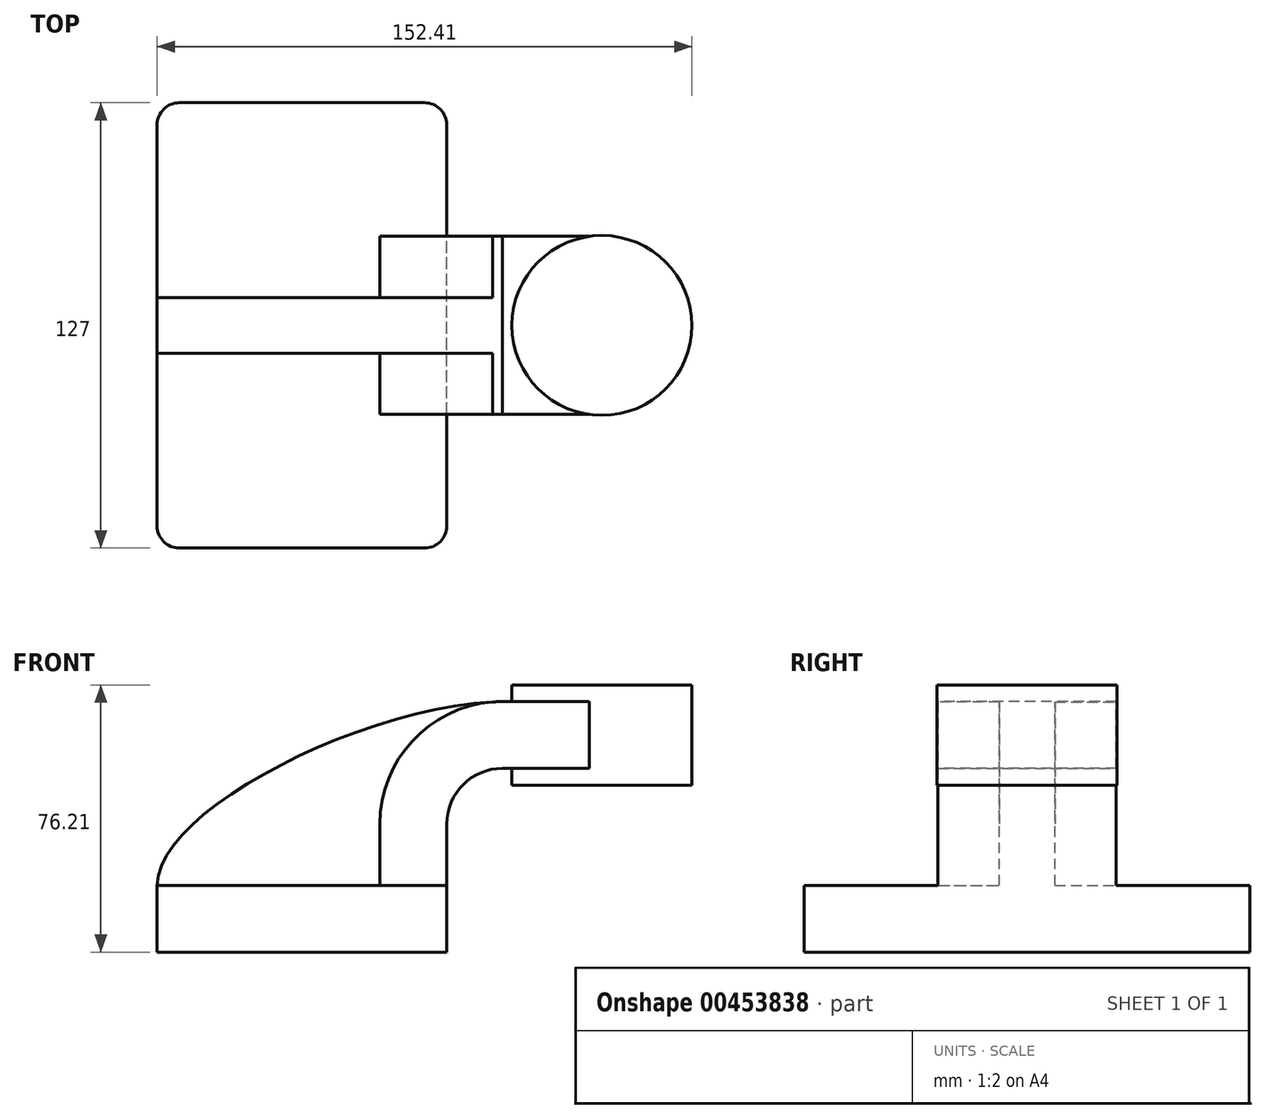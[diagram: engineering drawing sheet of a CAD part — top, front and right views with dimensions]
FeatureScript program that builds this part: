
annotation { "Feature Type Name" : "Feature", "Feature Type Description" : "" }
export const myFeature = defineFeature(function(context is Context, id is Id, definition is map)
    precondition{}
    {
        {
            var Q0;
            Q0=qCreatedBy(makeId("Front.planeOp"),FACE);
            var sketch = newSketch(context, id + "F0", { "sketchPlane" : qUnion([Q0])});
            skLineSegment(sketch, "E0.bottom", {"start": v(-41.28, 9.52) * mm, "end": v(41.27, 9.53) * mm});
            skLineSegment(sketch, "E0.top", {"start": v(-41.28, -9.53) * mm, "end": v(41.28, -9.53) * mm});
            skLineSegment(sketch, "E0.left", {"start": v(-41.28, 9.52) * mm, "end": v(-41.28, -9.53) * mm});
            skLineSegment(sketch, "E0.right", {"start": v(41.27, 9.53) * mm, "end": v(41.28, -9.52) * mm});
            skPoint(sketch, "E0.middle", {"position": v(0, 0) * mm});
            skLineSegment(sketch, "E1.bottom", {"start": v(111.12, 66.68) * mm, "end": v(60.32, 66.68) * mm});
            skLineSegment(sketch, "E1.top", {"start": v(111.12, 38.1) * mm, "end": v(60.32, 38.1) * mm});
            skLineSegment(sketch, "E1.left", {"start": v(111.12, 66.68) * mm, "end": v(111.12, 38.1) * mm});
            skLineSegment(sketch, "E1.right", {"start": v(60.32, 66.68) * mm, "end": v(60.32, 38.1) * mm});
            skPoint(sketch, "E1.middle", {"position": v(85.72, 52.39) * mm});
            skLineSegment(sketch, "E2", {"start": v(41.27, 9.53) * mm, "end": v(41.27, 27) * mm});
            skArc(sketch, "E3", {"start": v(41.27, 27) * mm, "mid": v(45.92, 38.23) * mm, "end": v(57.15, 42.88) * mm});
            skLineSegment(sketch, "E4", {"start": v(57.15, 42.88) * mm, "end": v(85.47, 42.88) * mm});
            skLineSegment(sketch, "E5.0", {"start": v(57.15, 61.93) * mm, "end": v(85.47, 61.93) * mm});
            skArc(sketch, "E5.1", {"start": v(22.22, 27) * mm, "mid": v(32.45, 51.7) * mm, "end": v(57.15, 61.93) * mm});
            skLineSegment(sketch, "E5.2", {"start": v(22.22, 9.53) * mm, "end": v(22.22, 27) * mm});
            skFitSpline(sketch, "E6", {"points": [v(-41.28, 9.52) * mm, v(57.15, 61.93) * mm], "startDerivative": vector(-0.59, 63.07) * mm, "endDerivative": vector(120.17, 2.95) * mm});
            skLineSegment(sketch, "E7", {"start": v(85.47, 42.88) * mm, "end": v(85.47, 61.93) * mm});
            skLineSegment(sketch, "E8", {"start": v(85.47, 42.88) * mm, "end": v(85.47, 38.1) * mm});
            skPoint(sketch, "E8.endSnap0", {"position": v(85.72, 38.1) * mm});
            skLineSegment(sketch, "E9", {"start": v(85.47, 61.93) * mm, "end": v(85.47, 66.68) * mm});
            skSolve(sketch);
        }
        {
            var Q0;
            Q0=makeQuery(id+"F0.imprint","IMPRINT",FACE,{"disambiguationData":[TD([[makeQuery(id+"F0.imprint","IMPRINT",EDGE,{"derivedFrom":sQuery(id+"F0.wireOp",EDGE,"E0.top")}),1.0]])]});
            extrude(context, id + "F1", {"entities" : qUnion([Q0]), "endBound" : BoundingType.SYMMETRIC, "depth" : 127 * mm});
        }
        {
            var Q0;
            {var subQ3=sQuery(id+"F0.wireOp",EDGE,"E5.2");Q0=makeQuery(id+"F0.imprint","IMPRINT",FACE,{"disambiguationData":[TD([[makeQuery(id+"F0.imprint","IMPRINT",EDGE,{"derivedFrom":subQ3}),1.0]])]});}
            extrude(context, id + "F2", {"entities" : qUnion([Q0]), "operationType" : NewBodyOperationType.ADD, "endBound" : BoundingType.SYMMETRIC, "depth" : 15.88 * mm});
        }
        {
            var Q0;
            {var subQ1=sQuery(id+"F0.wireOp",EDGE,"E2");Q0=makeQuery(id+"F0.imprint","IMPRINT",FACE,{"disambiguationData":[TD([[makeQuery(id+"F0.imprint","IMPRINT",EDGE,{"derivedFrom":subQ1}),1.0]])]});}
            var Q1;
            {var subQ5=sQuery(id+"F0.wireOp",EDGE,"E7");Q1=makeQuery(id+"F0.imprint","IMPRINT",FACE,{"disambiguationData":[TD([[makeQuery(id+"F0.imprint","IMPRINT",EDGE,{"derivedFrom":subQ5}),1.0]])]});}
            extrude(context, id + "F3", {"entities" : qUnion([Q0, Q1]), "operationType" : NewBodyOperationType.ADD, "endBound" : BoundingType.SYMMETRIC, "depth" : 50.8 * mm});
        }
        {
            var Q0;
            {var subQ0=sQuery(id+"F0.wireOp",EDGE,"E1.left");Q0=makeQuery(id+"F0.imprint","IMPRINT",FACE,{"disambiguationData":[TD([[makeQuery(id+"F0.imprint","IMPRINT",EDGE,{"derivedFrom":subQ0}),-1.0]])]});}
            var Q1;
            Q1=sQuery(id+"F0.wireOp",EDGE,"E8");
            revolve(context, id + "F4", {"operationType" : NewBodyOperationType.ADD, "entities" : qUnion([Q0]), "axis" : qUnion([Q1]), "revolveType" : RevolveType.FULL});
        }
        {
            var Q0;
            Q0=makeQuery(id+"F1.opExtrude","CAP_EDGE",EDGE,{"disambiguationData":[OSD([sQuery(id+"F0.wireOp",EDGE,"E0.left")])],"isStart":false});
            var Q1;
            Q1=makeQuery(id+"F1.opExtrude","CAP_EDGE",EDGE,{"disambiguationData":[OSD([sQuery(id+"F0.wireOp",EDGE,"E0.right")])],"isStart":false});
            var Q2;
            Q2=makeQuery(id+"F1.opExtrude","CAP_EDGE",EDGE,{"disambiguationData":[OSD([sQuery(id+"F0.wireOp",EDGE,"E0.right")])],"isStart":true});
            var Q3;
            Q3=makeQuery(id+"F1.opExtrude","CAP_EDGE",EDGE,{"disambiguationData":[OSD([sQuery(id+"F0.wireOp",EDGE,"E0.left")])],"isStart":true});
            fillet(context, id + "F5", {"entities" : qUnion([Q0, Q1, Q2, Q3]), "radius" : 6.35 * mm, "tangentPropagation" : true, "allowEdgeOverflow" : false});
        }
    });
